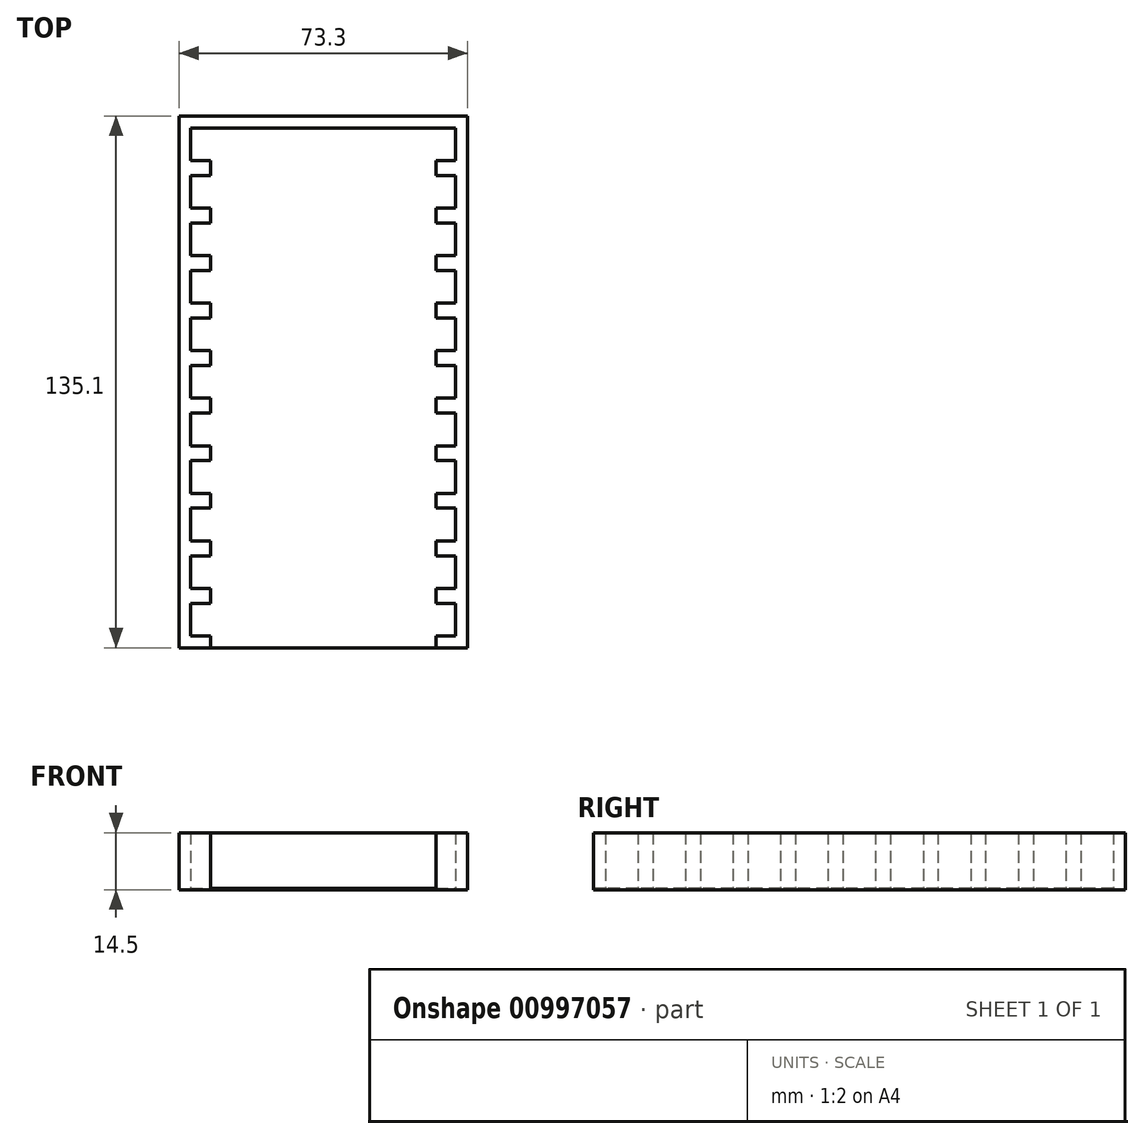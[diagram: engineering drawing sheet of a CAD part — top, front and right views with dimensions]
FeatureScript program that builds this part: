
annotation { "Feature Type Name" : "Feature", "Feature Type Description" : "" }
export const myFeature = defineFeature(function(context is Context, id is Id, definition is map)
    precondition{}
    {
        {
            var Q0;
            Q0=qCreatedBy(makeId("Top.planeOp"),FACE);
            var sketch = newSketch(context, id + "F0", { "sketchPlane" : qUnion([Q0])});
            skLineSegment(sketch, "E0.bottom", {"start": v(-33.65, 4.15) * mm, "end": v(33.65, 4.15) * mm});
            skLineSegment(sketch, "E0.top", {"start": v(-33.65, -4.15) * mm, "end": v(33.65, -4.15) * mm});
            skLineSegment(sketch, "E0.left", {"start": v(-33.65, 4.15) * mm, "end": v(-33.65, -4.15) * mm});
            skLineSegment(sketch, "E0.right", {"start": v(33.65, 4.15) * mm, "end": v(33.65, -4.15) * mm});
            skPoint(sketch, "E1", {"position": v(0, 4.15) * mm});
            skPoint(sketch, "E2", {"position": v(33.65, 0) * mm});
            skLineSegment(sketch, "E3.0.1.0", {"start": v(-33.65, 16.23) * mm, "end": v(33.65, 16.23) * mm});
            skLineSegment(sketch, "E3.0.1.1", {"start": v(-33.65, 16.23) * mm, "end": v(-33.65, 7.93) * mm});
            skLineSegment(sketch, "E3.0.1.2", {"start": v(-33.65, 7.93) * mm, "end": v(33.65, 7.93) * mm});
            skLineSegment(sketch, "E3.0.1.3", {"start": v(33.65, 16.23) * mm, "end": v(33.65, 7.93) * mm});
            skLineSegment(sketch, "E3.0.2.0", {"start": v(-33.65, 28.31) * mm, "end": v(33.65, 28.3) * mm});
            skLineSegment(sketch, "E3.0.2.1", {"start": v(-33.65, 28.31) * mm, "end": v(-33.65, 20.01) * mm});
            skLineSegment(sketch, "E3.0.2.2", {"start": v(-33.65, 20.01) * mm, "end": v(33.65, 20) * mm});
            skLineSegment(sketch, "E3.0.2.3", {"start": v(33.65, 28.31) * mm, "end": v(33.65, 20) * mm});
            skLineSegment(sketch, "E3.0.3.0", {"start": v(-33.65, 40.4) * mm, "end": v(33.65, 40.39) * mm});
            skLineSegment(sketch, "E3.0.3.1", {"start": v(-33.65, 40.4) * mm, "end": v(-33.65, 32.1) * mm});
            skLineSegment(sketch, "E3.0.3.2", {"start": v(-33.65, 32.1) * mm, "end": v(33.65, 32.1) * mm});
            skLineSegment(sketch, "E3.0.3.3", {"start": v(33.65, 40.4) * mm, "end": v(33.65, 32.09) * mm});
            skLineSegment(sketch, "E3.0.4.0", {"start": v(-33.65, 52.47) * mm, "end": v(33.65, 52.47) * mm});
            skLineSegment(sketch, "E3.0.4.1", {"start": v(-33.65, 52.47) * mm, "end": v(-33.65, 44.17) * mm});
            skLineSegment(sketch, "E3.0.4.2", {"start": v(-33.65, 44.17) * mm, "end": v(33.65, 44.17) * mm});
            skLineSegment(sketch, "E3.0.4.3", {"start": v(33.65, 52.47) * mm, "end": v(33.65, 44.17) * mm});
            skLineSegment(sketch, "E3.0.5.0", {"start": v(-33.65, 64.55) * mm, "end": v(33.65, 64.55) * mm});
            skLineSegment(sketch, "E3.0.5.1", {"start": v(-33.65, 64.55) * mm, "end": v(-33.65, 56.25) * mm});
            skLineSegment(sketch, "E3.0.5.2", {"start": v(-33.65, 56.25) * mm, "end": v(33.65, 56.25) * mm});
            skLineSegment(sketch, "E3.0.5.3", {"start": v(33.65, 64.55) * mm, "end": v(33.65, 56.25) * mm});
            skLineSegment(sketch, "E3.0.6.0", {"start": v(-33.65, 76.63) * mm, "end": v(33.65, 76.63) * mm});
            skLineSegment(sketch, "E3.0.6.1", {"start": v(-33.65, 76.63) * mm, "end": v(-33.65, 68.33) * mm});
            skLineSegment(sketch, "E3.0.6.2", {"start": v(-33.65, 68.33) * mm, "end": v(33.65, 68.33) * mm});
            skLineSegment(sketch, "E3.0.6.3", {"start": v(33.65, 76.63) * mm, "end": v(33.65, 68.33) * mm});
            skLineSegment(sketch, "E3.0.7.0", {"start": v(-33.65, 88.7) * mm, "end": v(33.65, 88.7) * mm});
            skLineSegment(sketch, "E3.0.7.1", {"start": v(-33.65, 88.7) * mm, "end": v(-33.65, 80.4) * mm});
            skLineSegment(sketch, "E3.0.7.2", {"start": v(-33.65, 80.4) * mm, "end": v(33.65, 80.4) * mm});
            skLineSegment(sketch, "E3.0.7.3", {"start": v(33.65, 88.7) * mm, "end": v(33.65, 80.4) * mm});
            skLineSegment(sketch, "E3.0.8.0", {"start": v(-33.65, 100.8) * mm, "end": v(33.65, 100.8) * mm});
            skLineSegment(sketch, "E3.0.8.1", {"start": v(-33.65, 100.8) * mm, "end": v(-33.65, 92.5) * mm});
            skLineSegment(sketch, "E3.0.8.2", {"start": v(-33.65, 92.5) * mm, "end": v(33.65, 92.5) * mm});
            skLineSegment(sketch, "E3.0.8.3", {"start": v(33.65, 100.8) * mm, "end": v(33.65, 92.5) * mm});
            skLineSegment(sketch, "E3.0.9.0", {"start": v(-33.65, 112.87) * mm, "end": v(33.65, 112.87) * mm});
            skLineSegment(sketch, "E3.0.9.1", {"start": v(-33.65, 112.87) * mm, "end": v(-33.65, 104.57) * mm});
            skLineSegment(sketch, "E3.0.9.2", {"start": v(-33.65, 104.57) * mm, "end": v(33.65, 104.57) * mm});
            skLineSegment(sketch, "E3.0.9.3", {"start": v(33.65, 112.87) * mm, "end": v(33.65, 104.57) * mm});
            skLineSegment(sketch, "E3.0.10.0", {"start": v(-33.65, 124.95) * mm, "end": v(33.65, 124.95) * mm});
            skLineSegment(sketch, "E3.0.10.1", {"start": v(-33.65, 124.95) * mm, "end": v(-33.65, 116.65) * mm});
            skLineSegment(sketch, "E3.0.10.2", {"start": v(-33.65, 116.65) * mm, "end": v(33.65, 116.65) * mm});
            skLineSegment(sketch, "E3.0.10.3", {"start": v(33.65, 124.95) * mm, "end": v(33.65, 116.65) * mm});
            skLineSegment(sketch, "E3.direction1", {"start": v(-33.65, 4.15) * mm, "end": v(-8.65, 4.15) * mm, "construction": true});
            skLineSegment(sketch, "E3.direction2", {"start": v(-33.65, 4.15) * mm, "end": v(-33.65, 16.23) * mm, "construction": true});
            skLineSegment(sketch, "E4.bottom", {"start": v(-36.65, -7.15) * mm, "end": v(36.65, -7.15) * mm});
            skLineSegment(sketch, "E4.top", {"start": v(-36.65, 127.95) * mm, "end": v(36.65, 127.95) * mm});
            skLineSegment(sketch, "E4.left", {"start": v(-36.65, -7.15) * mm, "end": v(-36.65, 127.95) * mm});
            skLineSegment(sketch, "E4.right", {"start": v(36.65, -7.15) * mm, "end": v(36.65, 127.95) * mm});
            skLineSegment(sketch, "E5.bottom", {"start": v(-28.65, 124.95) * mm, "end": v(28.65, 124.95) * mm});
            skLineSegment(sketch, "E5.top", {"start": v(-28.65, -7.15) * mm, "end": v(28.65, -7.15) * mm});
            skLineSegment(sketch, "E5.left", {"start": v(-28.65, 124.95) * mm, "end": v(-28.65, -7.15) * mm});
            skLineSegment(sketch, "E5.right", {"start": v(28.65, 124.95) * mm, "end": v(28.65, -7.15) * mm});
            skPoint(sketch, "E6", {"position": v(0, -7.15) * mm});
            skPoint(sketch, "E6.positionSnap0", {"position": v(0, -7.15) * mm});
            skPoint(sketch, "E6.positionSnap1", {"position": v(0, -4.15) * mm});
            skSolve(sketch);
        }
        {
            var Q0;
            {var subQ57=sQuery(id+"F0.wireOp",EDGE,"E0.left");Q0=makeQuery(id+"F0.imprint","IMPRINT",FACE,{"disambiguationData":[TD([[makeQuery(id+"F0.imprint","IMPRINT",EDGE,{"derivedFrom":subQ57}),-1.0]])]});}
            extrude(context, id + "F1", {"entities" : qUnion([Q0]), "depth" : 14.5 * mm, "offsetDistance" : 25 * mm});
        }
        {
            var Q0;
            Q0=makeQuery(id+"F1.opExtrude","CAP_FACE",FACE,{"disambiguationData":[OSD([sQuery(id+"F0.wireOp",EDGE,"E0.bottom"),sQuery(id+"F0.wireOp",EDGE,"E0.top"),sQuery(id+"F0.wireOp",EDGE,"E0.left"),sQuery(id+"F0.wireOp",EDGE,"E0.right"),sQuery(id+"F0.wireOp",EDGE,"E3.0.1.0"),sQuery(id+"F0.wireOp",EDGE,"E3.0.1.1"),sQuery(id+"F0.wireOp",EDGE,"E3.0.1.2"),sQuery(id+"F0.wireOp",EDGE,"E3.0.1.3"),sQuery(id+"F0.wireOp",EDGE,"E3.0.2.0"),sQuery(id+"F0.wireOp",EDGE,"E3.0.2.1"),sQuery(id+"F0.wireOp",EDGE,"E3.0.2.2"),sQuery(id+"F0.wireOp",EDGE,"E3.0.2.3"),sQuery(id+"F0.wireOp",EDGE,"E3.0.3.0"),sQuery(id+"F0.wireOp",EDGE,"E3.0.3.1"),sQuery(id+"F0.wireOp",EDGE,"E3.0.3.2"),sQuery(id+"F0.wireOp",EDGE,"E3.0.3.3"),sQuery(id+"F0.wireOp",EDGE,"E3.0.4.0"),sQuery(id+"F0.wireOp",EDGE,"E3.0.4.1"),sQuery(id+"F0.wireOp",EDGE,"E3.0.4.2"),sQuery(id+"F0.wireOp",EDGE,"E3.0.4.3"),sQuery(id+"F0.wireOp",EDGE,"E3.0.5.0"),sQuery(id+"F0.wireOp",EDGE,"E3.0.5.1"),sQuery(id+"F0.wireOp",EDGE,"E3.0.5.2"),sQuery(id+"F0.wireOp",EDGE,"E3.0.5.3"),sQuery(id+"F0.wireOp",EDGE,"E3.0.6.0"),sQuery(id+"F0.wireOp",EDGE,"E3.0.6.1"),sQuery(id+"F0.wireOp",EDGE,"E3.0.6.2"),sQuery(id+"F0.wireOp",EDGE,"E3.0.6.3"),sQuery(id+"F0.wireOp",EDGE,"E3.0.7.0"),sQuery(id+"F0.wireOp",EDGE,"E3.0.7.1"),sQuery(id+"F0.wireOp",EDGE,"E3.0.7.2"),sQuery(id+"F0.wireOp",EDGE,"E3.0.7.3"),sQuery(id+"F0.wireOp",EDGE,"E3.0.8.0"),sQuery(id+"F0.wireOp",EDGE,"E3.0.8.1"),sQuery(id+"F0.wireOp",EDGE,"E3.0.8.2"),sQuery(id+"F0.wireOp",EDGE,"E3.0.8.3"),sQuery(id+"F0.wireOp",EDGE,"E3.0.9.0"),sQuery(id+"F0.wireOp",EDGE,"E3.0.9.1"),sQuery(id+"F0.wireOp",EDGE,"E3.0.9.2"),sQuery(id+"F0.wireOp",EDGE,"E3.0.9.3"),sQuery(id+"F0.wireOp",EDGE,"E3.0.10.0"),sQuery(id+"F0.wireOp",EDGE,"E3.0.10.1"),sQuery(id+"F0.wireOp",EDGE,"E3.0.10.2"),sQuery(id+"F0.wireOp",EDGE,"E3.0.10.3"),sQuery(id+"F0.wireOp",EDGE,"E4.bottom"),sQuery(id+"F0.wireOp",EDGE,"E4.top"),sQuery(id+"F0.wireOp",EDGE,"E4.left"),sQuery(id+"F0.wireOp",EDGE,"E4.right"),sQuery(id+"F0.wireOp",EDGE,"E5.bottom"),sQuery(id+"F0.wireOp",EDGE,"E5.left"),sQuery(id+"F0.wireOp",EDGE,"E5.right")])],"isStart":true});
            var sketch = newSketch(context, id + "F2", { "sketchPlane" : qUnion([Q0])});
            skLineSegment(sketch, "E7.bottom", {"start": v(36.65, -127.95) * mm, "end": v(-36.65, -127.95) * mm});
            skLineSegment(sketch, "E7.top", {"start": v(36.65, 7.15) * mm, "end": v(-36.65, 7.15) * mm});
            skLineSegment(sketch, "E7.left", {"start": v(36.65, -127.95) * mm, "end": v(36.65, 7.15) * mm});
            skLineSegment(sketch, "E7.right", {"start": v(-36.65, -127.95) * mm, "end": v(-36.65, 7.15) * mm});
            skSolve(sketch);
        }
        {
            var Q0;
            {var subQ38=sQuery(id+"F0.wireOp",EDGE,"E0.left");Q0=makeQuery(id+"F2.imprint","IMPRINT",FACE,{"disambiguationData":[TD([[makeQuery(id+"F2.imprint","IMPRINT",EDGE,{"derivedFrom":makeQuery(id+"F1.opExtrude","CAP_EDGE",EDGE,{"disambiguationData":[OSD([subQ38])],"isStart":true})}),-1.0]])]});}
            extrude(context, id + "F3", {"entities" : qUnion([Q0]), "operationType" : NewBodyOperationType.ADD, "depth" : -.4 * mm, "offsetDistance" : 25 * mm});
        }
    });
